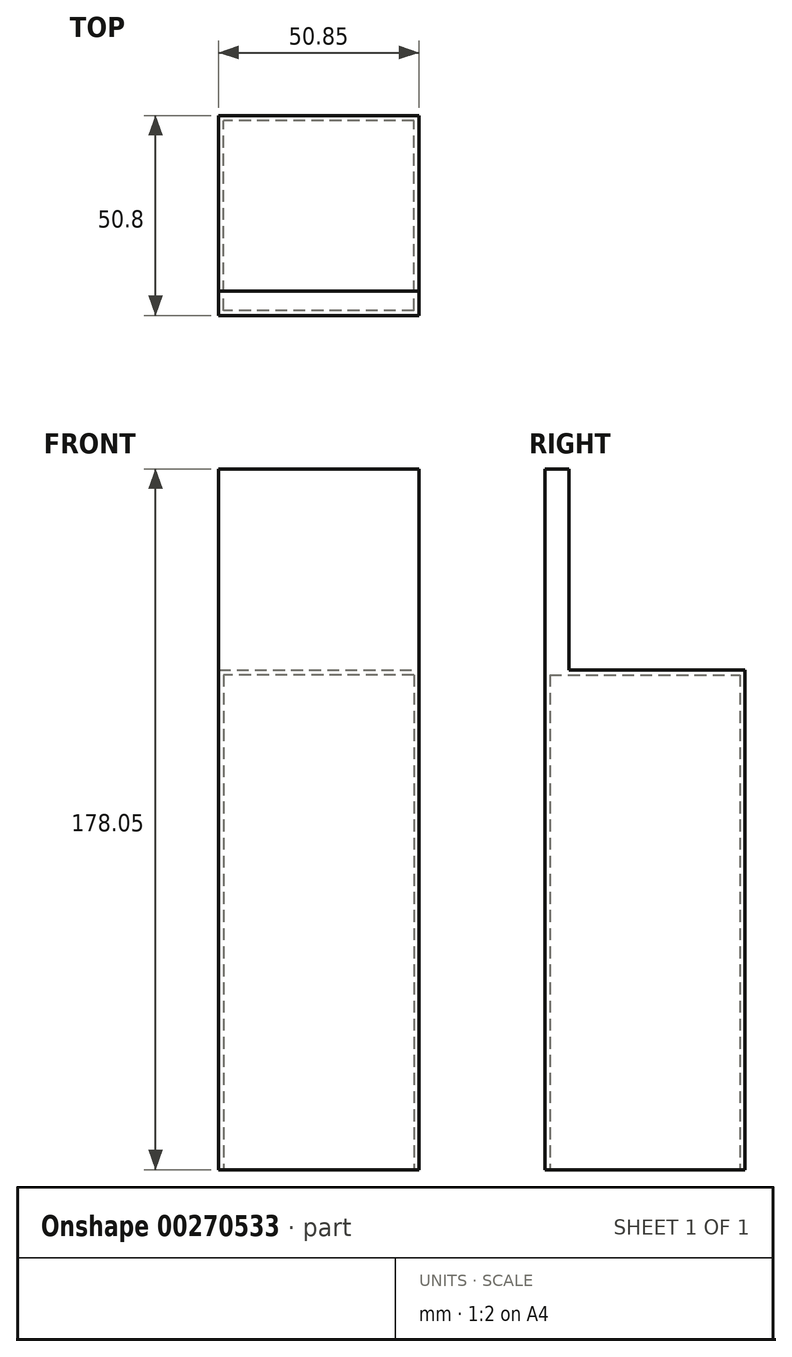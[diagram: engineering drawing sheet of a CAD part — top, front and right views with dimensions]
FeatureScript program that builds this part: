
annotation { "Feature Type Name" : "Feature", "Feature Type Description" : "" }
export const myFeature = defineFeature(function(context is Context, id is Id, definition is map)
    precondition{}
    {
        {
            var Q0;
            Q0=qCreatedBy(makeId("Right.planeOp"),FACE);
            var sketch = newSketch(context, id + "F0", { "sketchPlane" : qUnion([Q0])});
            skLineSegment(sketch, "E0.bottom", {"start": v(-48, 64.06) * mm, "end": v(2.8, 64.06) * mm});
            skLineSegment(sketch, "E0.top", {"start": v(-48, -62.94) * mm, "end": v(2.8, -62.94) * mm});
            skLineSegment(sketch, "E0.left", {"start": v(-48, 64.06) * mm, "end": v(-48, -62.94) * mm});
            skLineSegment(sketch, "E0.right", {"start": v(2.8, 64.06) * mm, "end": v(2.8, -62.94) * mm});
            skSolve(sketch);
        }
        {
            var Q0;
            Q0=qSketchRegion(id+"F0",true);
            extrude(context, id + "F1", {"entities" : qUnion([Q0]), "depth" : 50.85 * mm});
        }
        {
            var Q0;
            Q0=makeQuery(id+"F1.opExtrude","SWEPT_FACE",FACE,{"disambiguationData":[OSD([sQuery(id+"F0.wireOp",EDGE,"E0.top")])]});
            shell(context, id + "F2", {"entities" : qUnion([Q0]), "thickness" : 1.27 * mm});
        }
        {
            var Q0;
            Q0=makeQuery(id+"F1.opExtrude","SWEPT_FACE",FACE,{"disambiguationData":[OSD([sQuery(id+"F0.wireOp",EDGE,"E0.bottom")])]});
            var sketch = newSketch(context, id + "F3", { "sketchPlane" : qUnion([Q0])});
            skLineSegment(sketch, "E1.bottom", {"start": v(0, -48) * mm, "end": v(50.85, -48) * mm});
            skLineSegment(sketch, "E1.top", {"start": v(0, -41.84) * mm, "end": v(50.85, -41.84) * mm});
            skLineSegment(sketch, "E1.left", {"start": v(0, -48) * mm, "end": v(0, -41.84) * mm});
            skLineSegment(sketch, "E1.right", {"start": v(50.85, -48) * mm, "end": v(50.85, -41.84) * mm});
            skSolve(sketch);
        }
        {
            var Q0;
            Q0=makeQuery(id+"F3.imprint","IMPRINT",FACE,{"disambiguationData":[TD([[makeQuery(id+"F3.imprint","IMPRINT",EDGE,{"derivedFrom":sQuery(id+"F3.wireOp",EDGE,"E1.bottom")}),-1.0]])]});
            extrude(context, id + "F4", {"entities" : qUnion([Q0]), "operationType" : NewBodyOperationType.ADD, "depth" : 25.4 * mm});
        }
        {
            var Q0;
            Q0=makeQuery(id+"F4.opExtrude","CAP_FACE",FACE,{"disambiguationData":[OSD([sQuery(id+"F3.wireOp",EDGE,"E1.bottom"),sQuery(id+"F3.wireOp",EDGE,"E1.top"),sQuery(id+"F3.wireOp",EDGE,"E1.left"),sQuery(id+"F3.wireOp",EDGE,"E1.right")])],"isStart":false});
            extrude(context, id + "F5", {"entities" : qUnion([Q0]), "operationType" : NewBodyOperationType.ADD, "depth" : 25.65 * mm});
        }
    });
